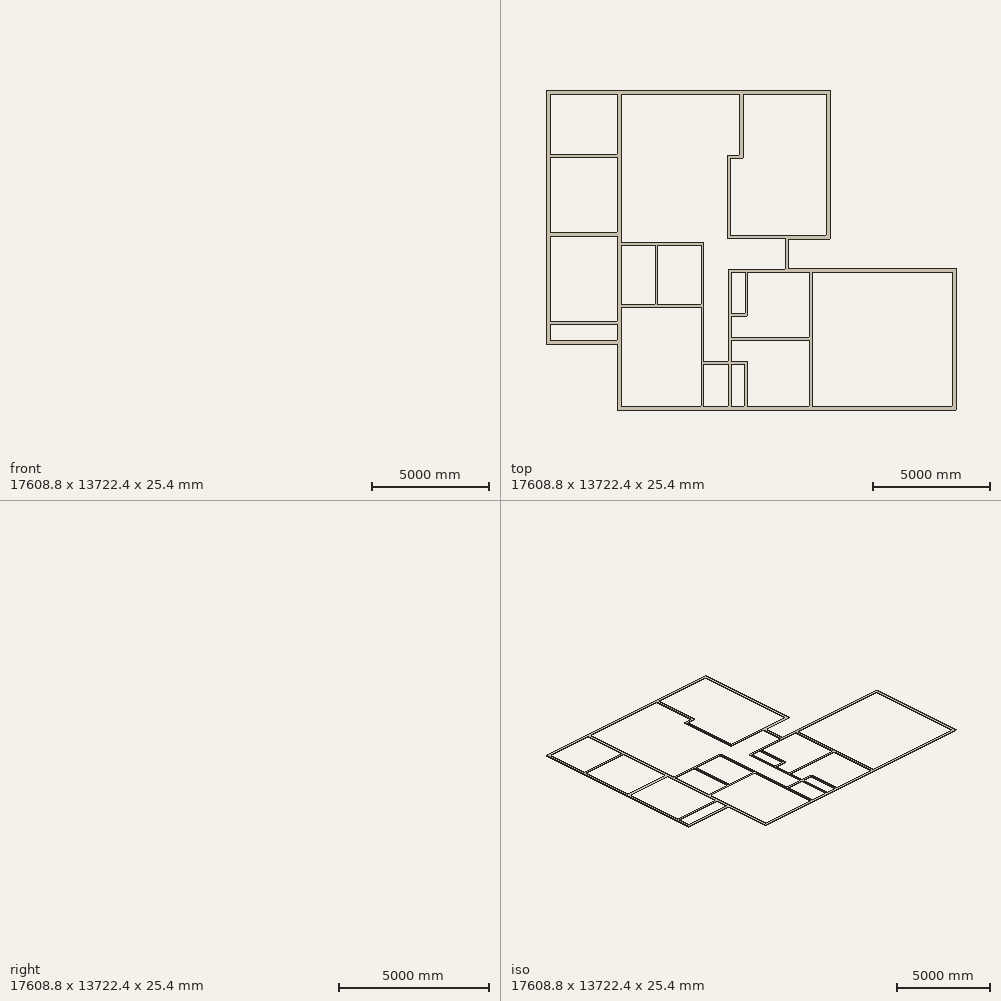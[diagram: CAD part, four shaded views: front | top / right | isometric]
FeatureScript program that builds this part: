
annotation { "Feature Type Name" : "Feature", "Feature Type Description" : "" }
export const myFeature = defineFeature(function(context is Context, id is Id, definition is map)
    precondition{}
    {
        {
            var Q0;
            Q0=qCreatedBy(makeId("Top.planeOp"),FACE);
            var sketch = newSketch(context, id + "F0", { "sketchPlane" : qUnion([Q0])});
            skLineSegment(sketch, "E0", {"start": v(0, 0) * mm, "end": v(-3568.7, 0) * mm});
            skLineSegment(sketch, "E1", {"start": v(-11849.1, 0) * mm, "end": v(-11849.1, -2590.8) * mm});
            skLineSegment(sketch, "E2", {"start": v(-11849.1, -10553.7) * mm, "end": v(-8978.9, -10553.7) * mm});
            skLineSegment(sketch, "E3", {"start": v(-8813.8, -10553.7) * mm, "end": v(-8813.8, -13392.15) * mm});
            skLineSegment(sketch, "E4", {"start": v(-8813.8, -13392.15) * mm, "end": v(5429.53, -13392.15) * mm});
            skLineSegment(sketch, "E5", {"start": v(5429.53, -13392.15) * mm, "end": v(5429.53, -7626.35) * mm});
            skLineSegment(sketch, "E6", {"start": v(5429.53, -7626.35) * mm, "end": v(-1765.3, -7626.35) * mm});
            skLineSegment(sketch, "E7", {"start": v(0, -6070.6) * mm, "end": v(0, 0) * mm});
            skLineSegment(sketch, "E8.0", {"start": v(165.1, -6235.7) * mm, "end": v(165.1, 165.1) * mm});
            skLineSegment(sketch, "E8.2", {"start": v(165.1, 165.1) * mm, "end": v(-12014.2, 165.1) * mm});
            skLineSegment(sketch, "E8.4", {"start": v(5594.63, -7461.25) * mm, "end": v(-1600.2, -7461.25) * mm});
            skLineSegment(sketch, "E8.5", {"start": v(5594.63, -13557.25) * mm, "end": v(5594.63, -7461.25) * mm});
            skLineSegment(sketch, "E8.6", {"start": v(-12014.2, 165.1) * mm, "end": v(-12014.2, -10718.8) * mm});
            skLineSegment(sketch, "E8.7", {"start": v(-12014.2, -10718.8) * mm, "end": v(-8978.9, -10718.8) * mm});
            skLineSegment(sketch, "E8.8", {"start": v(-8978.9, -10718.8) * mm, "end": v(-8978.9, -13557.25) * mm});
            skLineSegment(sketch, "E8.9", {"start": v(-8978.9, -13557.25) * mm, "end": v(5594.63, -13557.25) * mm});
            skLineSegment(sketch, "E9", {"start": v(-8978.9, 0) * mm, "end": v(-8978.9, -2590.8) * mm});
            skLineSegment(sketch, "E10", {"start": v(-8978.9, -2590.8) * mm, "end": v(-11849.1, -2590.8) * mm});
            skLineSegment(sketch, "E11", {"start": v(-8813.8, 0) * mm, "end": v(-8813.8, -10553.7) * mm});
            skLineSegment(sketch, "E12", {"start": v(-11849.1, -2705.1) * mm, "end": v(-8978.9, -2705.1) * mm});
            skLineSegment(sketch, "E13", {"start": v(-8978.9, -2705.1) * mm, "end": v(-8978.9, -5918.2) * mm});
            skLineSegment(sketch, "E14", {"start": v(-8978.9, -10553.7) * mm, "end": v(-11849.1, -10553.7) * mm});
            skLineSegment(sketch, "E15", {"start": v(-11849.1, -5918.2) * mm, "end": v(-8978.9, -5918.2) * mm});
            skLineSegment(sketch, "E16", {"start": v(-8978.9, -6083.3) * mm, "end": v(-8978.9, -10553.7) * mm});
            skLineSegment(sketch, "E17.trimOffspring", {"start": v(-11849.1, -2705.1) * mm, "end": v(-11849.1, -5918.2) * mm});
            skLineSegment(sketch, "E18", {"start": v(-11849.1, -6083.3) * mm, "end": v(-8978.9, -6083.3) * mm});
            skLineSegment(sketch, "E19.trimOffspring", {"start": v(-11849.1, -6083.3) * mm, "end": v(-11849.1, -10553.7) * mm});
            skLineSegment(sketch, "E20", {"start": v(-3568.7, 0) * mm, "end": v(-3568.7, -2746.38) * mm});
            skLineSegment(sketch, "E21", {"start": v(-3568.7, -2746.38) * mm, "end": v(-4114.8, -2746.38) * mm});
            skLineSegment(sketch, "E22", {"start": v(-4114.8, -2746.38) * mm, "end": v(-4114.8, -6070.6) * mm});
            skLineSegment(sketch, "E23", {"start": v(-1600.2, -7461.25) * mm, "end": v(-1600.2, -6235.7) * mm});
            skLineSegment(sketch, "E24", {"start": v(-1765.3, -7512.05) * mm, "end": v(-1765.3, -6184.9) * mm});
            skLineSegment(sketch, "E25.trimOffspring", {"start": v(-1600.2, -6235.7) * mm, "end": v(165.1, -6235.7) * mm});
            skLineSegment(sketch, "E26", {"start": v(-3733.8, 0) * mm, "end": v(-3733.8, -2632.08) * mm});
            skLineSegment(sketch, "E27", {"start": v(-3733.8, -2632.08) * mm, "end": v(-4229.1, -2632.08) * mm});
            skLineSegment(sketch, "E28", {"start": v(-4229.1, -2632.08) * mm, "end": v(-4229.1, -6184.9) * mm});
            skLineSegment(sketch, "E29.trimOffspring", {"start": v(-3733.8, 0) * mm, "end": v(-11849.1, 0) * mm});
            skLineSegment(sketch, "E30", {"start": v(-5257.8, -6369.05) * mm, "end": v(-8813.8, -6369.05) * mm});
            skLineSegment(sketch, "E31", {"start": v(-8813.8, -6483.35) * mm, "end": v(-5372.1, -6483.35) * mm});
            skLineSegment(sketch, "E32", {"start": v(-5372.1, -6483.35) * mm, "end": v(-5372.1, -13392.15) * mm});
            skLineSegment(sketch, "E33", {"start": v(-5257.8, -6369.05) * mm, "end": v(-5257.8, -13392.15) * mm});
            skLineSegment(sketch, "E34", {"start": v(0, -6070.6) * mm, "end": v(-1765.3, -6070.6) * mm});
            skLineSegment(sketch, "E35", {"start": v(-1765.3, -6070.6) * mm, "end": v(-4114.8, -6070.6) * mm});
            skLineSegment(sketch, "E36", {"start": v(-1765.3, -6184.9) * mm, "end": v(-4229.1, -6184.9) * mm});
            skLineSegment(sketch, "E37", {"start": v(-5372.1, -9023.35) * mm, "end": v(-8813.8, -9023.35) * mm});
            skLineSegment(sketch, "E38", {"start": v(-8813.8, -9137.65) * mm, "end": v(-5372.1, -9137.65) * mm});
            skLineSegment(sketch, "E39", {"start": v(-7340.6, -6483.35) * mm, "end": v(-7340.6, -9023.35) * mm});
            skLineSegment(sketch, "E40", {"start": v(-7226.3, -6483.35) * mm, "end": v(-7226.3, -9023.35) * mm});
            skLineSegment(sketch, "E41", {"start": v(-5257.8, -11461.75) * mm, "end": v(-3381.37, -11461.75) * mm});
            skLineSegment(sketch, "E42", {"start": v(-3381.37, -11461.75) * mm, "end": v(-3381.37, -13392.15) * mm});
            skLineSegment(sketch, "E43", {"start": v(-5257.8, -11576.05) * mm, "end": v(-3495.67, -11576.05) * mm});
            skLineSegment(sketch, "E44", {"start": v(-3495.67, -11576.05) * mm, "end": v(-3495.67, -13392.15) * mm});
            skLineSegment(sketch, "E45", {"start": v(-4203.7, -11576.05) * mm, "end": v(-4203.7, -13392.15) * mm});
            skLineSegment(sketch, "E46", {"start": v(-4089.4, -13392.15) * mm, "end": v(-4089.4, -11576.05) * mm});
            skLineSegment(sketch, "E47", {"start": v(-4203.7, -11461.75) * mm, "end": v(-4203.7, -7512.05) * mm});
            skLineSegment(sketch, "E48", {"start": v(-4089.4, -11461.75) * mm, "end": v(-4089.4, -7626.35) * mm});
            skLineSegment(sketch, "E49", {"start": v(-1765.3, -7626.35) * mm, "end": v(-4089.4, -7626.35) * mm});
            skLineSegment(sketch, "E50", {"start": v(-1765.3, -7512.05) * mm, "end": v(-4203.7, -7512.05) * mm});
            skLineSegment(sketch, "E51", {"start": v(-3486.15, -7626.35) * mm, "end": v(-3486.15, -9398) * mm});
            skLineSegment(sketch, "E52", {"start": v(-3486.15, -9398) * mm, "end": v(-4089.4, -9398) * mm});
            skLineSegment(sketch, "E53", {"start": v(-3371.85, -7626.35) * mm, "end": v(-3371.85, -9512.3) * mm});
            skLineSegment(sketch, "E54", {"start": v(-3371.85, -9512.3) * mm, "end": v(-4089.4, -9512.3) * mm});
            skLineSegment(sketch, "E55", {"start": v(-4089.4, -10445.75) * mm, "end": v(-739.77, -10445.75) * mm});
            skLineSegment(sketch, "E56", {"start": v(-4089.4, -10560.05) * mm, "end": v(-739.77, -10560.05) * mm});
            skLineSegment(sketch, "E57", {"start": v(-11849.1, -9740.9) * mm, "end": v(-8978.9, -9740.9) * mm});
            skLineSegment(sketch, "E58", {"start": v(-11849.1, -9855.2) * mm, "end": v(-8978.9, -9855.2) * mm});
            skLineSegment(sketch, "E59", {"start": v(-739.77, -7626.35) * mm, "end": v(-739.77, -13392.15) * mm});
            skLineSegment(sketch, "E60", {"start": v(-574.67, -7626.35) * mm, "end": v(-574.67, -13392.15) * mm});
            skSolve(sketch);
        }
        {
            var Q0;
            Q0 = qSketchRegion(id + "F0", true);
            var Q1;
            {var subQ5=sQuery(id+"F0.wireOp",EDGE,"E60");Q1=makeQuery(id+"F0.imprint","IMPRINT",FACE,{"disambiguationData":[TD([[makeQuery(id+"F0.imprint","IMPRINT",EDGE,{"derivedFrom":subQ5}),-1.0]])]});}
            var Q2;
            {var subQ0=sQuery(id+"F0.wireOp",EDGE,"E55");Q2=makeQuery(id+"F0.imprint","IMPRINT",FACE,{"disambiguationData":[TD([[makeQuery(id+"F0.imprint","IMPRINT",EDGE,{"derivedFrom":subQ0}),-1.0]])]});}
            var Q3;
            {var subQ1=sQuery(id+"F0.wireOp",EDGE,"E51");Q3=makeQuery(id+"F0.imprint","IMPRINT",FACE,{"disambiguationData":[TD([[makeQuery(id+"F0.imprint","IMPRINT",EDGE,{"derivedFrom":subQ1}),1.0]])]});}
            var Q4;
            {var subQ7=sQuery(id+"F0.wireOp",EDGE,"E42");Q4=makeQuery(id+"F0.imprint","IMPRINT",FACE,{"disambiguationData":[TD([[makeQuery(id+"F0.imprint","IMPRINT",EDGE,{"derivedFrom":subQ7}),-1.0]])]});}
            var Q5;
            {var subQ0=sQuery(id+"F0.wireOp",EDGE,"E45");Q5=makeQuery(id+"F0.imprint","IMPRINT",FACE,{"disambiguationData":[TD([[makeQuery(id+"F0.imprint","IMPRINT",EDGE,{"derivedFrom":subQ0}),1.0]])]});}
            var Q6;
            {var subQ1=sQuery(id+"F0.wireOp",EDGE,"E30");Q6=makeQuery(id+"F0.imprint","IMPRINT",FACE,{"disambiguationData":[TD([[makeQuery(id+"F0.imprint","IMPRINT",EDGE,{"derivedFrom":subQ1}),1.0]])]});}
            var Q7;
            {var subQ0=sQuery(id+"F0.wireOp",EDGE,"E57");Q7=makeQuery(id+"F0.imprint","IMPRINT",FACE,{"disambiguationData":[TD([[makeQuery(id+"F0.imprint","IMPRINT",EDGE,{"derivedFrom":subQ0}),-1.0]])]});}
            var Q8;
            {var subQ5=sQuery(id+"F0.wireOp",EDGE,"E38");Q8=makeQuery(id+"F0.imprint","IMPRINT",FACE,{"disambiguationData":[TD([[makeQuery(id+"F0.imprint","IMPRINT",EDGE,{"derivedFrom":subQ5}),1.0]])]});}
            var Q9;
            {var subQ0=sQuery(id+"F0.wireOp",EDGE,"E39");Q9=makeQuery(id+"F0.imprint","IMPRINT",FACE,{"disambiguationData":[TD([[makeQuery(id+"F0.imprint","IMPRINT",EDGE,{"derivedFrom":subQ0}),1.0]])]});}
            extrude(context, id + "F1", {"entities" : qUnion([Q0, Q1, Q2, Q3, Q4, Q5, Q6, Q7, Q8, Q9]), "depth" : 25.4 * mm, "offsetDistance" : 25.4 * mm});
        }
    });
